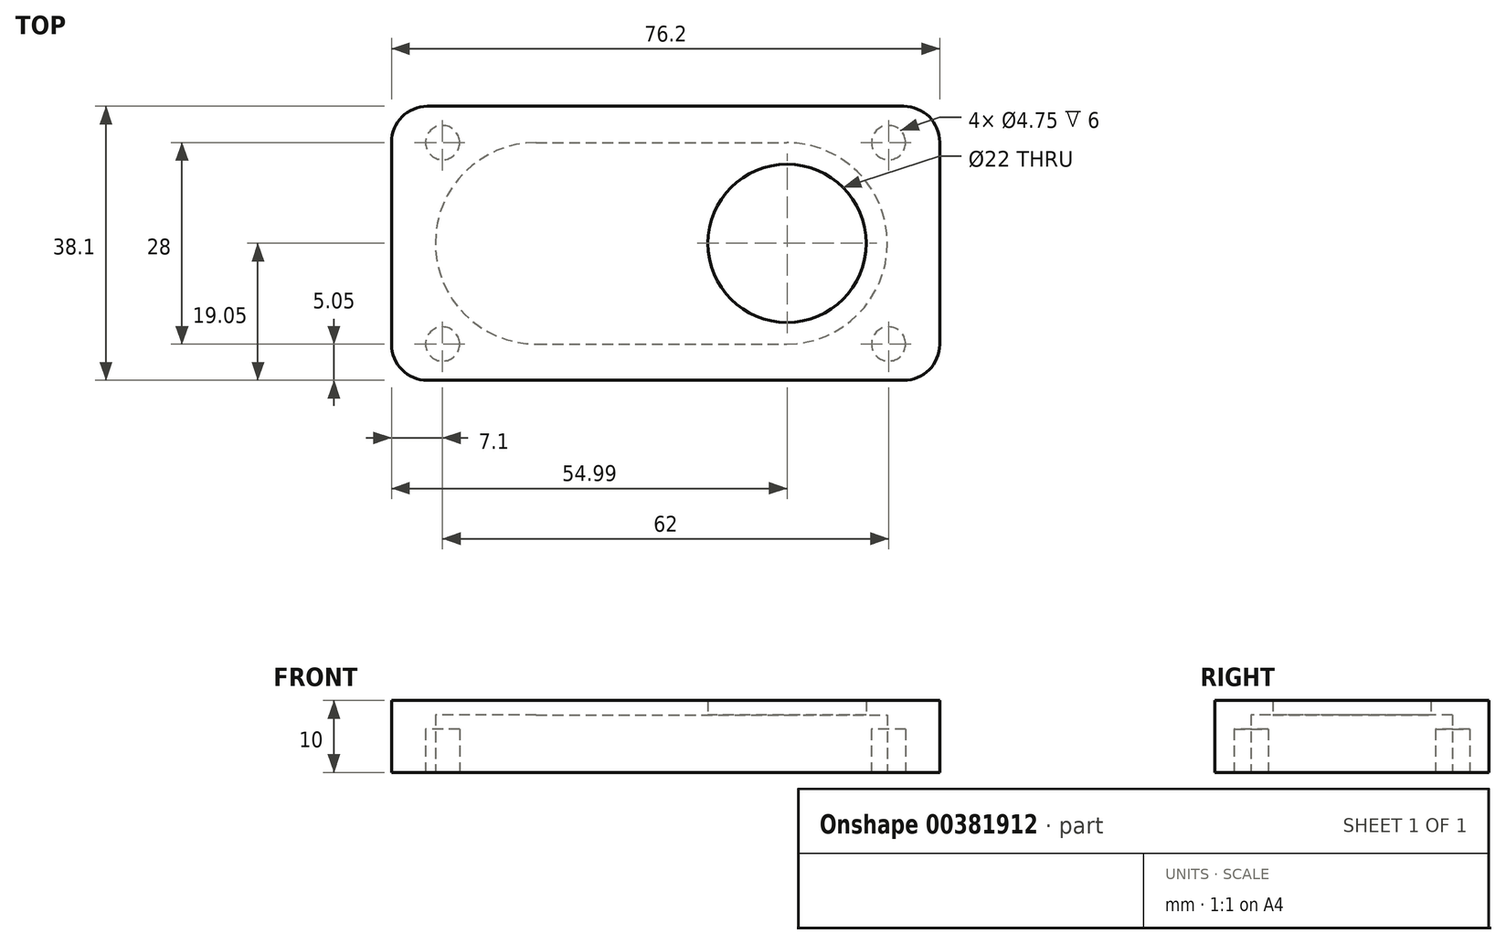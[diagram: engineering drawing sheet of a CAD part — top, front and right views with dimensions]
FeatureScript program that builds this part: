
annotation { "Feature Type Name" : "Feature", "Feature Type Description" : "" }
export const myFeature = defineFeature(function(context is Context, id is Id, definition is map)
    precondition{}
    {
        {
            var Q0;
            Q0=qCreatedBy(makeId("Top.planeOp"),FACE);
            var sketch = newSketch(context, id + "F0", { "sketchPlane" : qUnion([Q0])});
            skLineSegment(sketch, "E0.bottom", {"start": v(-33.1, 19.05) * mm, "end": v(33.1, 19.05) * mm});
            skLineSegment(sketch, "E0.top", {"start": v(-33.1, -19.05) * mm, "end": v(33.1, -19.05) * mm});
            skLineSegment(sketch, "E0.left", {"start": v(-38.1, 14.05) * mm, "end": v(-38.1, -14.05) * mm});
            skLineSegment(sketch, "E0.right", {"start": v(38.1, 14.05) * mm, "end": v(38.1, -14.05) * mm});
            skPoint(sketch, "E0.middle", {"position": v(0, 0) * mm});
            skPoint(sketch, "E1.visualSharp", {"position": v(-38.1, 19.05) * mm});
            skArc(sketch, "E1.filletArc", {"start": v(-33.1, 19.05) * mm, "mid": v(-36.64, 17.59) * mm, "end": v(-38.1, 14.05) * mm});
            skPoint(sketch, "E2.visualSharp", {"position": v(-38.1, -19.05) * mm});
            skArc(sketch, "E2.filletArc", {"start": v(-38.1, -14.05) * mm, "mid": v(-36.64, -17.59) * mm, "end": v(-33.1, -19.05) * mm});
            skPoint(sketch, "E3.visualSharp", {"position": v(38.1, -19.05) * mm});
            skArc(sketch, "E3.filletArc", {"start": v(33.1, -19.05) * mm, "mid": v(36.64, -17.59) * mm, "end": v(38.1, -14.05) * mm});
            skPoint(sketch, "E4.visualSharp", {"position": v(38.1, 19.05) * mm});
            skArc(sketch, "E4.filletArc", {"start": v(38.1, 14.05) * mm, "mid": v(36.64, 17.59) * mm, "end": v(33.1, 19.05) * mm});
            skSolve(sketch);
        }
        {
            var Q0;
            Q0=makeQuery(id+"F0.imprint","IMPRINT",FACE,{"disambiguationData":[TD([[makeQuery(id+"F0.imprint","IMPRINT",EDGE,{"derivedFrom":sQuery(id+"F0.wireOp",EDGE,"E0.bottom")}),-1.0]])]});
            extrude(context, id + "F1", {"entities" : qUnion([Q0]), "depth" : 10 * mm});
        }
        {
            var Q0;
            Q0=qCreatedBy(makeId("Top.planeOp"),FACE);
            var sketch = newSketch(context, id + "F2", { "sketchPlane" : qUnion([Q0])});
            skCircle(sketch, "E5", {"center": v(16.89, 0) * mm, "radius": 11 * mm});
            skSolve(sketch);
        }
        {
            var Q0;
            Q0=makeQuery(id+"F2.imprint","IMPRINT",FACE,{"disambiguationData":[TD([[makeQuery(id+"F2.imprint","IMPRINT",EDGE,{"derivedFrom":sQuery(id+"F2.wireOp",EDGE,"TaF6Fijp-NT3D-NpAD-COS4-qacth3kr2UEy.bottom")}),-1.0]])]});
            var Q1;
            Q1=makeQuery(id+"F2.imprint","IMPRINT",FACE,{"disambiguationData":[TD([[makeQuery(id+"F2.imprint","IMPRINT",EDGE,{"derivedFrom":sQuery(id+"F2.wireOp",EDGE,"c986f50b-f069-45bb-ac77-7a01fd66f314.filletArc")}),1.0]])]});
            var Q2;
            Q2=makeQuery(id+"F2.imprint","IMPRINT",FACE,{"disambiguationData":[TD([[makeQuery(id+"F2.imprint","IMPRINT",EDGE,{"derivedFrom":sQuery(id+"F2.wireOp",EDGE,"E5")}),1.0]])]});
            extrude(context, id + "F3", {"entities" : qUnion([Q0, Q1, Q2]), "operationType" : NewBodyOperationType.REMOVE, "oppositeDirection" : true, "depth" : -20 * mm});
        }
        {
            var Q0;
            Q0=qCreatedBy(makeId("Top.planeOp"),FACE);
            var sketch = newSketch(context, id + "F4", { "sketchPlane" : qUnion([Q0])});
            skCircle(sketch, "E6", {"center": v(-31, 14) * mm, "radius": 2.38 * mm});
            skCircle(sketch, "E7", {"center": v(-31, -14) * mm, "radius": 2.38 * mm});
            skCircle(sketch, "E8", {"center": v(31, 14) * mm, "radius": 2.38 * mm});
            skCircle(sketch, "E9", {"center": v(31, -14) * mm, "radius": 2.38 * mm});
            skLineSegment(sketch, "E10.bottom", {"start": v(-31, -14) * mm, "end": v(31, -14) * mm});
            skLineSegment(sketch, "E10.top", {"start": v(-31, 14) * mm, "end": v(31, 14) * mm});
            skLineSegment(sketch, "E10.left", {"start": v(-31, -14) * mm, "end": v(-31, 14) * mm});
            skLineSegment(sketch, "E10.right", {"start": v(31, -14) * mm, "end": v(31, 14) * mm});
            skPoint(sketch, "E10.middle", {"position": v(0, 0) * mm});
            skSolve(sketch);
        }
        {
            var Q0;
            Q0=makeQuery(id+"F4.imprint","IMPRINT",FACE,{"disambiguationData":[TD([[makeQuery(id+"F4.imprint","IMPRINT",EDGE,{"derivedFrom":sQuery(id+"F4.wireOp",EDGE,"E9")}),1.0]])]});
            var Q1;
            Q1=makeQuery(id+"F4.imprint","IMPRINT",FACE,{"disambiguationData":[TD([[makeQuery(id+"F4.imprint","IMPRINT",EDGE,{"derivedFrom":sQuery(id+"F4.wireOp",EDGE,"E7")}),1.0]])]});
            var Q2;
            Q2=makeQuery(id+"F4.imprint","IMPRINT",FACE,{"disambiguationData":[TD([[makeQuery(id+"F4.imprint","IMPRINT",EDGE,{"derivedFrom":sQuery(id+"F4.wireOp",EDGE,"E6")}),1.0]])]});
            var Q3;
            Q3=makeQuery(id+"F4.imprint","IMPRINT",FACE,{"disambiguationData":[TD([[makeQuery(id+"F4.imprint","IMPRINT",EDGE,{"derivedFrom":sQuery(id+"F4.wireOp",EDGE,"E8")}),1.0]])]});
            var Q4;
            Q4=sQuery(id+"F4.wireOp",EDGE,"E6");
            var Q5;
            Q5=sQuery(id+"F4.wireOp",EDGE,"E7");
            var Q6;
            Q6=sQuery(id+"F4.wireOp",EDGE,"E8");
            var Q7;
            Q7=sQuery(id+"F4.wireOp",EDGE,"E9");
            extrude(context, id + "F5", {"entities" : qUnion([Q0, Q1, Q2, Q3]), "operationType" : NewBodyOperationType.REMOVE, "surfaceEntities" : qUnion([Q4, Q5, Q6, Q7]), "oppositeDirection" : true, "depth" : -6 * mm});
        }
        {
            var Q0;
            Q0=qCreatedBy(makeId("Top.planeOp"),FACE);
            var sketch = newSketch(context, id + "F6", { "sketchPlane" : qUnion([Q0])});
            skLineSegment(sketch, "E11.bottom", {"start": v(-18, 14) * mm, "end": v(16.83, 14) * mm});
            skLineSegment(sketch, "E11.top", {"start": v(-18, -14) * mm, "end": v(16.83, -14) * mm});
            skLineSegment(sketch, "E11.left", {"start": v(-32, 0) * mm, "end": v(-32, 0) * mm});
            skLineSegment(sketch, "E11.right", {"start": v(30.83, 0) * mm, "end": v(30.83, 0) * mm});
            skPoint(sketch, "E11.middle", {"position": v(0, 0) * mm});
            skPoint(sketch, "E12.visualSharp", {"position": v(-32, 14) * mm});
            skArc(sketch, "E12.filletArc", {"start": v(-18, 14) * mm, "mid": v(-27.9, 9.9) * mm, "end": v(-32, 0) * mm});
            skPoint(sketch, "E13.visualSharp", {"position": v(-32, -14) * mm});
            skArc(sketch, "E13.filletArc", {"start": v(-32, 0) * mm, "mid": v(-27.9, -9.9) * mm, "end": v(-18, -14) * mm});
            skPoint(sketch, "E14.visualSharp", {"position": v(32, -14) * mm});
            skArc(sketch, "E14.filletArc", {"start": v(16.83, -14) * mm, "mid": v(26.73, -9.9) * mm, "end": v(30.83, 0) * mm});
            skPoint(sketch, "E15.visualSharp", {"position": v(32, 14) * mm});
            skArc(sketch, "E15.filletArc", {"start": v(30.83, 0) * mm, "mid": v(26.73, 9.9) * mm, "end": v(16.83, 14) * mm});
            skSolve(sketch);
        }
        {
            var Q0;
            Q0=makeQuery(id+"F6.imprint","IMPRINT",FACE,{"disambiguationData":[TD([[makeQuery(id+"F6.imprint","IMPRINT",EDGE,{"derivedFrom":sQuery(id+"F6.wireOp",EDGE,"E11.bottom")}),-1.0]])]});
            extrude(context, id + "F7", {"entities" : qUnion([Q0]), "operationType" : NewBodyOperationType.REMOVE, "oppositeDirection" : true, "depth" : -8 * mm});
        }
    });
